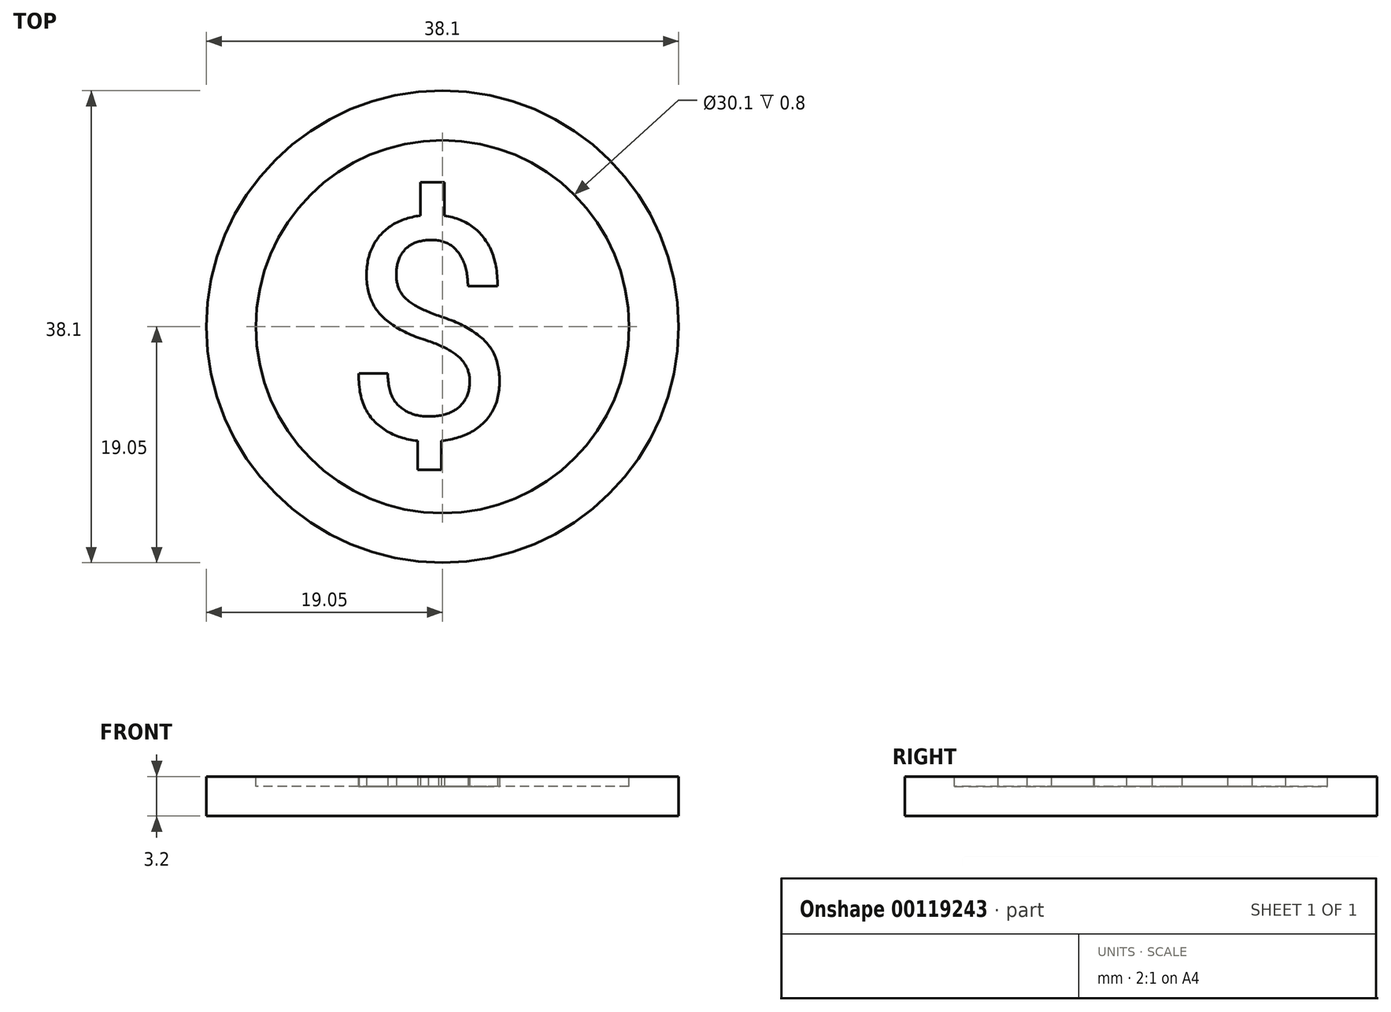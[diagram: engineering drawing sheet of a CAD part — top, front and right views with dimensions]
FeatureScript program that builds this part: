
annotation { "Feature Type Name" : "Feature", "Feature Type Description" : "" }
export const myFeature = defineFeature(function(context is Context, id is Id, definition is map)
    precondition{}
    {
        {
            var Q0;
            Q0=qCreatedBy(makeId("Top.planeOp"),FACE);
            var sketch = newSketch(context, id + "F0", { "sketchPlane" : qUnion([Q0])});
            skCircle(sketch, "E0", {"center": v(0, 0) * mm, "radius": 19.05 * mm});
            skSolve(sketch);
        }
        {
            var Q0;
            Q0 = qSketchRegion(id + "F0", true);
            extrude(context, id + "F1", {"entities" : qUnion([Q0]), "depth" : 3.2 * mm});
        }
        {
            var Q0;
            Q0=makeQuery(id+"F1.opExtrude","CAP_FACE",FACE,{"disambiguationData":[OSD([sQuery(id+"F0.wireOp",EDGE,"E0")])],"isStart":false});
            var sketch = newSketch(context, id + "F2", { "sketchPlane" : qUnion([Q0])});
            skCircle(sketch, "E1", {"center": v(0, 0) * mm, "radius": 15.05 * mm});
            skSolve(sketch);
        }
        {
            var Q0;
            Q0=makeQuery(id+"F2.imprint","IMPRINT",FACE,{"disambiguationData":[TD([[makeQuery(id+"F2.imprint","IMPRINT",EDGE,{"derivedFrom":sQuery(id+"F2.wireOp",EDGE,"E1")}),1.0]])]});
            extrude(context, id + "F3", {"entities" : qUnion([Q0]), "operationType" : NewBodyOperationType.REMOVE, "oppositeDirection" : true, "depth" : .8 * mm});
        }
        {
            var Q0;
            Q0=makeQuery(id+"F3.boolean.opBoolean","COPY",FACE,{"derivedFrom":makeQuery(id+"F3.opExtrude","CAP_FACE",FACE,{"disambiguationData":[OSD([sQuery(id+"F2.wireOp",EDGE,"E1")])],"isStart":false})});
            var sketch = newSketch(context, id + "F4", { "sketchPlane" : qUnion([Q0])});
            skText(sketch, "E2", { "text": "$", "fontName": "RobotoSlab-Regular.ttf"});
            const initialGuessF4  = {"E2": [-0.00775, -0.009, 1, 0, 0.018]};
            skSetInitialGuess(sketch, initialGuessF4);
            skSolve(sketch);
        }
        {
            var Q0;
            Q0 = qSketchRegion(id + "F4", true);
            extrude(context, id + "F5", {"entities" : qUnion([Q0]), "operationType" : NewBodyOperationType.ADD, "depth" : .8 * mm});
        }
    });
